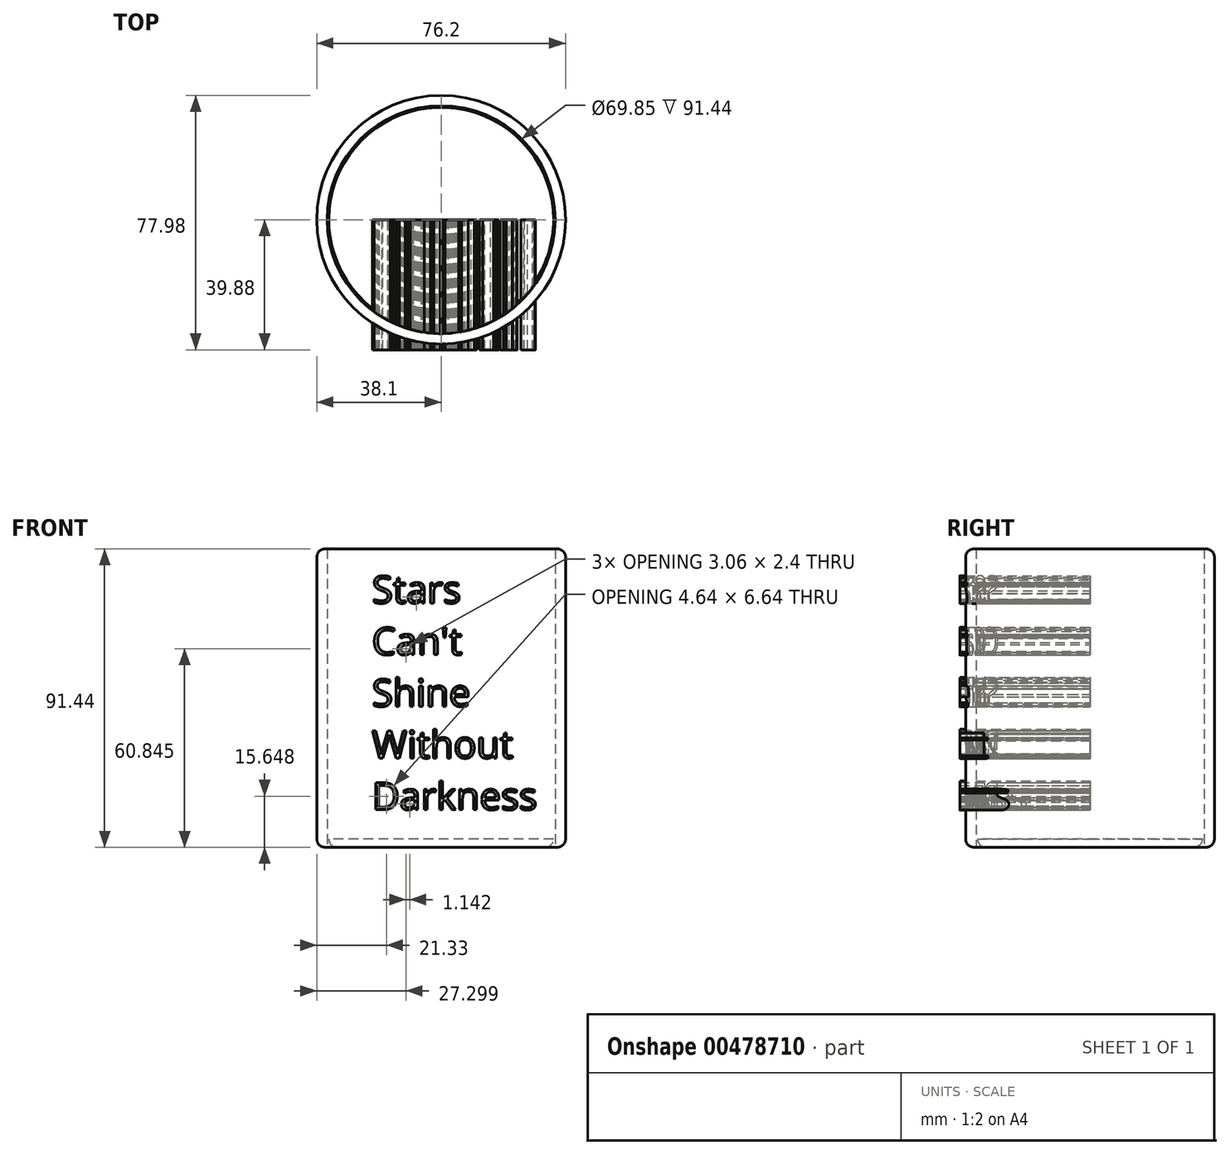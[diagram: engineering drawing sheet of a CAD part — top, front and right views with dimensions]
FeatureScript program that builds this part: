
annotation { "Feature Type Name" : "Feature", "Feature Type Description" : "" }
export const myFeature = defineFeature(function(context is Context, id is Id, definition is map)
    precondition{}
    {
        {
            var Q0;
            Q0=qCreatedBy(makeId("Top.planeOp"),FACE);
            var sketch = newSketch(context, id + "F0", { "sketchPlane" : qUnion([Q0])});
            skCircle(sketch, "E0", {"center": v(0, 0) * mm, "radius": 34.93 * mm});
            skCircle(sketch, "E1", {"center": v(0, 0) * mm, "radius": 38.1 * mm});
            skSolve(sketch);
        }
        {
            var Q0;
            Q0 = qSketchRegion(id + "F0", true);
            extrude(context, id + "F1", {"entities" : qUnion([Q0]), "depth" : 91.44 * mm});
        }
        {
            var Q0;
            Q0=qCreatedBy(makeId("Top.planeOp"),FACE);
            var sketch = newSketch(context, id + "F2", { "sketchPlane" : qUnion([Q0])});
            skCircle(sketch, "E2", {"center": v(0, 0) * mm, "radius": 34.41 * mm});
            skSolve(sketch);
        }
        {
            var Q0;
            Q0 = qSketchRegion(id + "F2", true);
            extrude(context, id + "F3", {"entities" : qUnion([Q0]), "depth" : 2.54 * mm});
        }
        {
            var Q0;
            Q0=makeQuery(id+"F1.opExtrude","SWEPT_FACE",FACE,{"disambiguationData":[OSD([sQuery(id+"F0.wireOp",EDGE,"E1")])]});
            var Q1;
            Q1=makeQuery(id+"F3.opExtrude","CAP_EDGE",EDGE,{"disambiguationData":[OSD([sQuery(id+"F2.wireOp",EDGE,"E2")])],"isStart":true});
            fillet(context, id + "F4", {"entities" : qUnion([Q0, Q1]), "radius" : 2.54 * mm, "tangentPropagation" : true, "allowEdgeOverflow" : false});
        }
        {
            var Q0;
            Q0=qCreatedBy(makeId("Front.planeOp"),FACE);
            var sketch = newSketch(context, id + "F5", { "sketchPlane" : qUnion([Q0])});
            skText(sketch, "E3", { "text": "Stars \nCan\'t \nShine \nWithout \nDarkness", "fontName": "OpenSans-Regular.ttf"});
            skLineSegment(sketch, "E4", {"start": v(39.56, 88.93) * mm, "end": v(39.56, -3.95) * mm});
            skLineSegment(sketch, "E5", {"start": v(39.56, -3.95) * mm, "end": v(-35.54, -3.95) * mm});
            skLineSegment(sketch, "E6", {"start": v(-35.54, -3.95) * mm, "end": v(-16.43, -23.73) * mm});
            skLineSegment(sketch, "E7", {"start": v(-16.43, -23.73) * mm, "end": v(76.78, -23.73) * mm});
            skLineSegment(sketch, "E8", {"start": v(76.78, -23.73) * mm, "end": v(76.78, 89.26) * mm});
            skLineSegment(sketch, "E9", {"start": v(39.56, 88.93) * mm, "end": v(39.56, 96.97) * mm});
            skLineSegment(sketch, "E10", {"start": v(39.56, 96.97) * mm, "end": v(-33.03, 96.97) * mm});
            skLineSegment(sketch, "E11", {"start": v(-33.03, 96.97) * mm, "end": v(-11.57, 116.42) * mm});
            skLineSegment(sketch, "E12", {"start": v(-11.57, 116.42) * mm, "end": v(74.94, 116.42) * mm});
            skLineSegment(sketch, "E13", {"start": v(74.94, 116.42) * mm, "end": v(76.78, 79.54) * mm});
            const initialGuessF5  = {"E3": [-0.0212, 0.07481, 1, 0, 0.00838]};
            skSetInitialGuess(sketch, initialGuessF5);
            skSolve(sketch);
        }
        {
            var Q0;
            Q0 = qSketchRegion(id + "F5", true);
            extrude(context, id + "F6", {"entities" : qUnion([Q0]), "operationType" : NewBodyOperationType.ADD, "depth" : 39.88 * mm});
        }
        {
            var Q0;
            Q0=makeQuery(id+"F6.opExtrude","SWEPT_BODY",BODY,{"disambiguationData":[OSD([sQuery(id+"F5.wireOp",EDGE,"E4"),sQuery(id+"F5.wireOp",EDGE,"E5"),sQuery(id+"F5.wireOp",EDGE,"E6"),sQuery(id+"F5.wireOp",EDGE,"E7"),sQuery(id+"F5.wireOp",EDGE,"E8"),sQuery(id+"F5.wireOp",EDGE,"E9"),sQuery(id+"F5.wireOp",EDGE,"E10"),sQuery(id+"F5.wireOp",EDGE,"E11"),sQuery(id+"F5.wireOp",EDGE,"E12"),sQuery(id+"F5.wireOp",EDGE,"E13")])]});
            deleteBodies(context, id + "F7", {"entities" : qUnion([Q0])});
        }
    });
